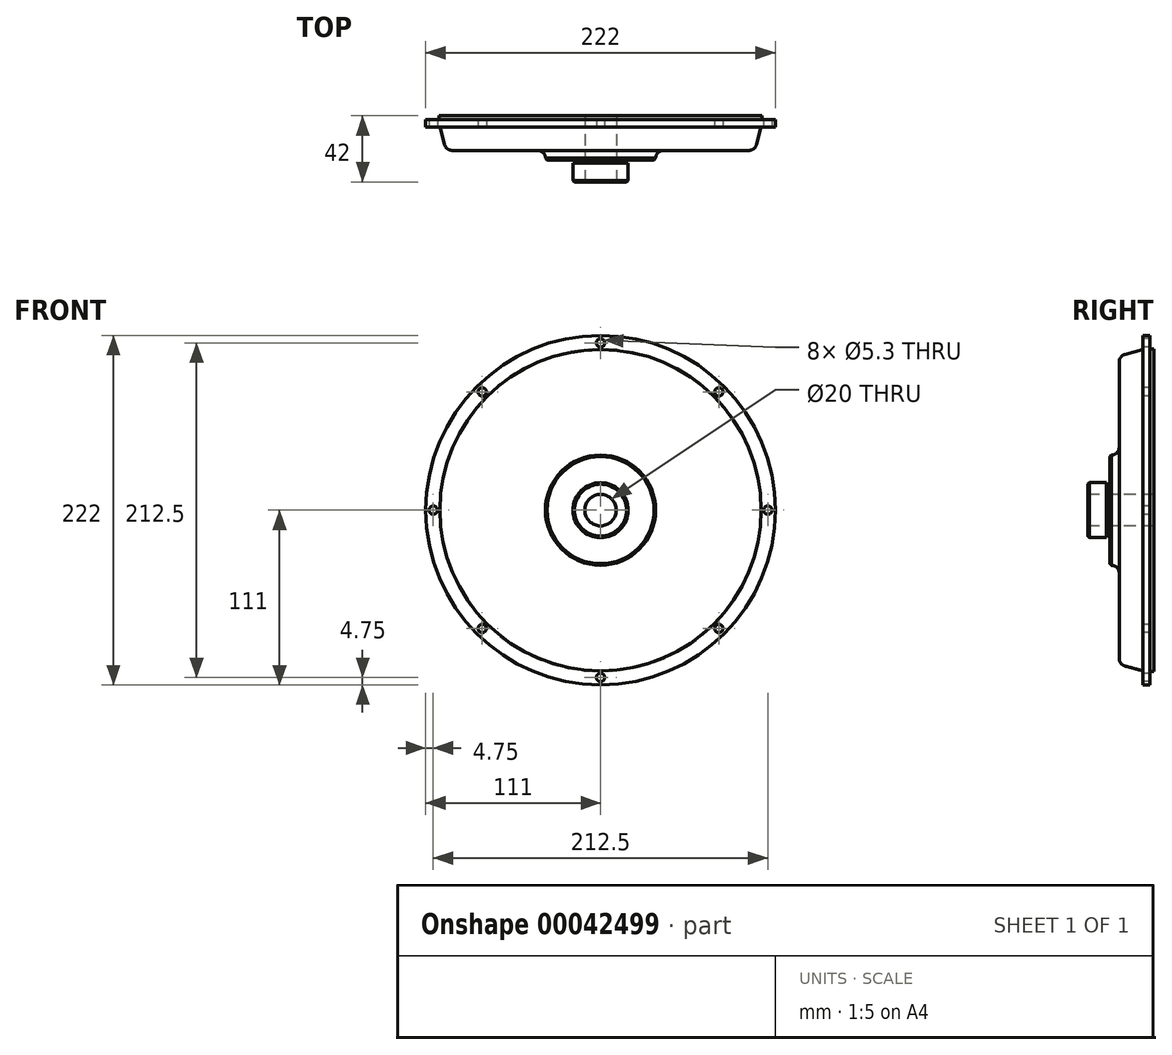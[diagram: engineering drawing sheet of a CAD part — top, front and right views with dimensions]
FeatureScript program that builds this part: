
annotation { "Feature Type Name" : "Feature", "Feature Type Description" : "" }
export const myFeature = defineFeature(function(context is Context, id is Id, definition is map)
    precondition{}
    {
        {
            var Q0;
            Q0=qCreatedBy(makeId("Right.planeOp"),FACE);
            var sketch = newSketch(context, id + "F0", { "sketchPlane" : qUnion([Q0])});
            skLineSegment(sketch, "E0", {"start": v(2.5, 102.5) * mm, "end": v(0, 102.5) * mm});
            skLineSegment(sketch, "E1", {"start": v(0, 102.5) * mm, "end": v(0, 111) * mm});
            skLineSegment(sketch, "E2", {"start": v(0, 111) * mm, "end": v(-4.6, 111) * mm});
            skLineSegment(sketch, "E3", {"start": v(-4.6, 111) * mm, "end": v(-4.6, 102) * mm});
            skLineSegment(sketch, "E4", {"start": v(-4.6, 102) * mm, "end": v(-15.8, 99) * mm});
            skLineSegment(sketch, "E5", {"start": v(-19.5, 94.17) * mm, "end": v(-19.5, 40) * mm});
            skLineSegment(sketch, "E6", {"start": v(-39.5, 16.5) * mm, "end": v(-39.5, 10) * mm});
            skLineSegment(sketch, "E7", {"start": v(-39.5, 10) * mm, "end": v(2.5, 10) * mm});
            skLineSegment(sketch, "E8", {"start": v(2.5, 10) * mm, "end": v(2.5, 102.5) * mm});
            skLineSegment(sketch, "E9", {"start": v(0, 0) * mm, "end": v(-52.31, 0) * mm, "construction": true});
            skPoint(sketch, "E10.visualSharp", {"position": v(-19.5, 98) * mm});
            skArc(sketch, "E10.filletArc", {"start": v(-15.8, 99) * mm, "mid": v(-18.47, 97.21) * mm, "end": v(-19.5, 94.17) * mm});
            skArc(sketch, "E11", {"start": v(-24.5, 35) * mm, "mid": v(-20.96, 36.46) * mm, "end": v(-19.5, 40) * mm});
            skLineSegment(sketch, "E12", {"start": v(-24.5, 35) * mm, "end": v(-25.5, 34) * mm});
            skLineSegment(sketch, "E13", {"start": v(-25.5, 34) * mm, "end": v(-25.5, 16.5) * mm});
            skLineSegment(sketch, "E14", {"start": v(-25.5, 16.5) * mm, "end": v(-27.5, 16.5) * mm});
            skLineSegment(sketch, "E15", {"start": v(-27.5, 16.5) * mm, "end": v(-27.5, 17.5) * mm});
            skLineSegment(sketch, "E16", {"start": v(-27.5, 17.5) * mm, "end": v(-38.5, 17.5) * mm});
            skLineSegment(sketch, "E17", {"start": v(-38.5, 17.5) * mm, "end": v(-39.5, 16.5) * mm});
            skSolve(sketch);
        }
        {
            var Q0;
            Q0=qSketchRegion(id+"F0",true);
            var Q1;
            Q1=sQuery(id+"F0.wireOp",EDGE,"E9");
            revolve(context, id + "F1", {"entities" : qUnion([Q0]), "axis" : qUnion([Q1]), "revolveType" : RevolveType.FULL, "oppositeDirection" : true});
        }
        {
            var Q0;
            Q0=makeQuery(id+"F1.opRevolve","SWEPT_FACE",FACE,{"disambiguationData":[OSD([sQuery(id+"F0.wireOp",EDGE,"E3")])]});
            var sketch = newSketch(context, id + "F2", { "sketchPlane" : qUnion([Q0])});
            skCircle(sketch, "E18", {"center": v(-106.25, 0) * mm, "radius": 2.65 * mm});
            skCircle(sketch, "E19.1.0", {"center": v(-75.13, -75.13) * mm, "radius": 2.65 * mm});
            skCircle(sketch, "E19.2.0", {"center": v(0, -106.25) * mm, "radius": 2.65 * mm});
            skCircle(sketch, "E19.3.0", {"center": v(75.13, -75.13) * mm, "radius": 2.65 * mm});
            skCircle(sketch, "E19.4.0", {"center": v(106.25, 0) * mm, "radius": 2.65 * mm});
            skCircle(sketch, "E19.5.0", {"center": v(75.13, 75.13) * mm, "radius": 2.65 * mm});
            skCircle(sketch, "E19.6.0", {"center": v(0, 106.25) * mm, "radius": 2.65 * mm});
            skCircle(sketch, "E19.7.0", {"center": v(-75.13, 75.13) * mm, "radius": 2.65 * mm});
            skPoint(sketch, "E19.center", {"position": v(0, 0) * mm});
            skSolve(sketch);
        }
        {
            var Q0;
            Q0=qSketchRegion(id+"F2",true);
            extrude(context, id + "F3", {"entities" : qUnion([Q0]), "operationType" : NewBodyOperationType.REMOVE, "endBound" : BoundingType.THROUGH_ALL, "oppositeDirection" : true, "depth" : 25 * mm});
        }
    });
